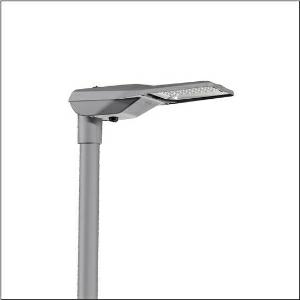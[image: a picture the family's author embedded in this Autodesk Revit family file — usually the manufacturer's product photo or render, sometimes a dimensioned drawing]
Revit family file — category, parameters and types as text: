
# Revit family: streetlight_sl_21_iq_mini___st1_0a_5xe2d41y08hb_48d2
name_source: partatom
category: Lighting Fixtures
units: mm (PartAtom-declared; Revit-internal decimal feet)

## family parameters
Cut with Voids When Loaded = No
Host = Face
Light Source = No
Part Type = Normal
Room Calculation Point = No
Round Connector Dimension = Use Diameter
Shared = No

## types (1)
- --- (1 x LED, 10080 lm, 71 W, 4000K)
    Apparent Load = 71 VA
    CIE Flux Codes = 37 72 97 100 100
    Color Rendering = 70
    Color Temperature = 4000K
    Default Elevation = 1800 mm
    Description = Streetlight SL 21 iQ mini, mast luminaire, primary light control with lens, of PMMA, primary optical cover: cover, of toughened safety glass, transparent, light distribution: ST1.0a, light emission: direct distribution, primary light characteristic: asymmetric, installation type: post-top, side-entry, LED, High Power LED, rated luminous flux: 10.080lm, luminous efficacy: 142lm/W, light colour: 740, colour temperature: 4000K, control gear: iQ-Street Remote, D4i with power reduction, control: pre-setting: logarithmic dimming characteristic, Street-Remote, Auto-Match, Temp-Guard, Lumen-Switch, Night-Set, Smart-Wire, Light-Fading, Desk-Remote (wireless, voltage-free reading and setting of iQ features in the workshop via application-optimized NFC function/RFID function), optimised constant luminous flux control (CLO 2.0), mains connection: 220..240V, AC, 50/60Hz, start of lifetime: 71W, end of service life: 75W, reduction: 31W, luminaire housing, of diecast aluminium, powder-coated, SITECO metallic grey (DB 702S), corrosivity category C5 high according to DIN EN ISO 12944, please order mast flange separately, inclination adjustable: 0°, 5°, 10°, 15°, sealing non-destructively replaceable, multi-level sealing system, length: 628mm, width: 235mm, height: 110mm, mast flange for spigot size: 42mm (side-entry): 5XC10008XM4, 60/48mm (side-entry/post-top): 5XC10108XM2, 76/60mm (side-entry/post-top): 5XC10108XM1, mounting height: 4..8m, Smart Interface below and above, protection rating (complete): IP66, insulation class (complete): insulation class II (safety insulation), certification: CE, ENEC, ENEC+, VDE, impact resistance: IK10, permissible operating ambient temperature for outdoor applications: -40..+50°C, standard-compliant lighting for roads and squares, packaging unit: 1 piece

Light Distribution: ST1.0a
    Height = 110 mm
    Lamp = 1 x LED
    Lamp Light Flux = 10080 lm
    Lamp Power = 71 W
    Lamp count = 1
    Length = 625 mm
    Luminous efficacy = 142 lm/W
    Manufacturer = Siteco
    ModVariant = No
    Model = 5XE2D41Y08HB
    Number of Poles = 1
    OnlyDefault = Yes
    Power Factor = 1
    Product Name = Streetlight SL 21 iQ mini | ST1.0a
    Product group = mast luminaire | pylon top
    ProductGroupID = 6100
    Protection Class = Protection class II
    Protection Degree = IP 66
    RLX_Detail_Level = 1
    RLX_Emergency_Light_Flux = 0 lm
    RLX_Emergency_Type = 0
    RLX_Emergency_Type_DB = No
    RlxData = <blob elided: 92749 chars, md5=75146627>
    Socket = socket
    Standby Power = 0 W
    System Light Flux = 10080 lm
    System Power = 71 W
    Type Comments = factory setting: luminous flux: 100 % | dim-lin: 254 | 716 mA
    Type Image = l_1003514.jpg
    URL = http://relux.com
    VarID = @adj_114843
    Voltage = 0 V
    Weight = 0.00 kg
    Width = 234 mm

## geometry (parser evidence)
native form markers: Blend x4, Sweep x11
no freeform markers — native parametric forms only
